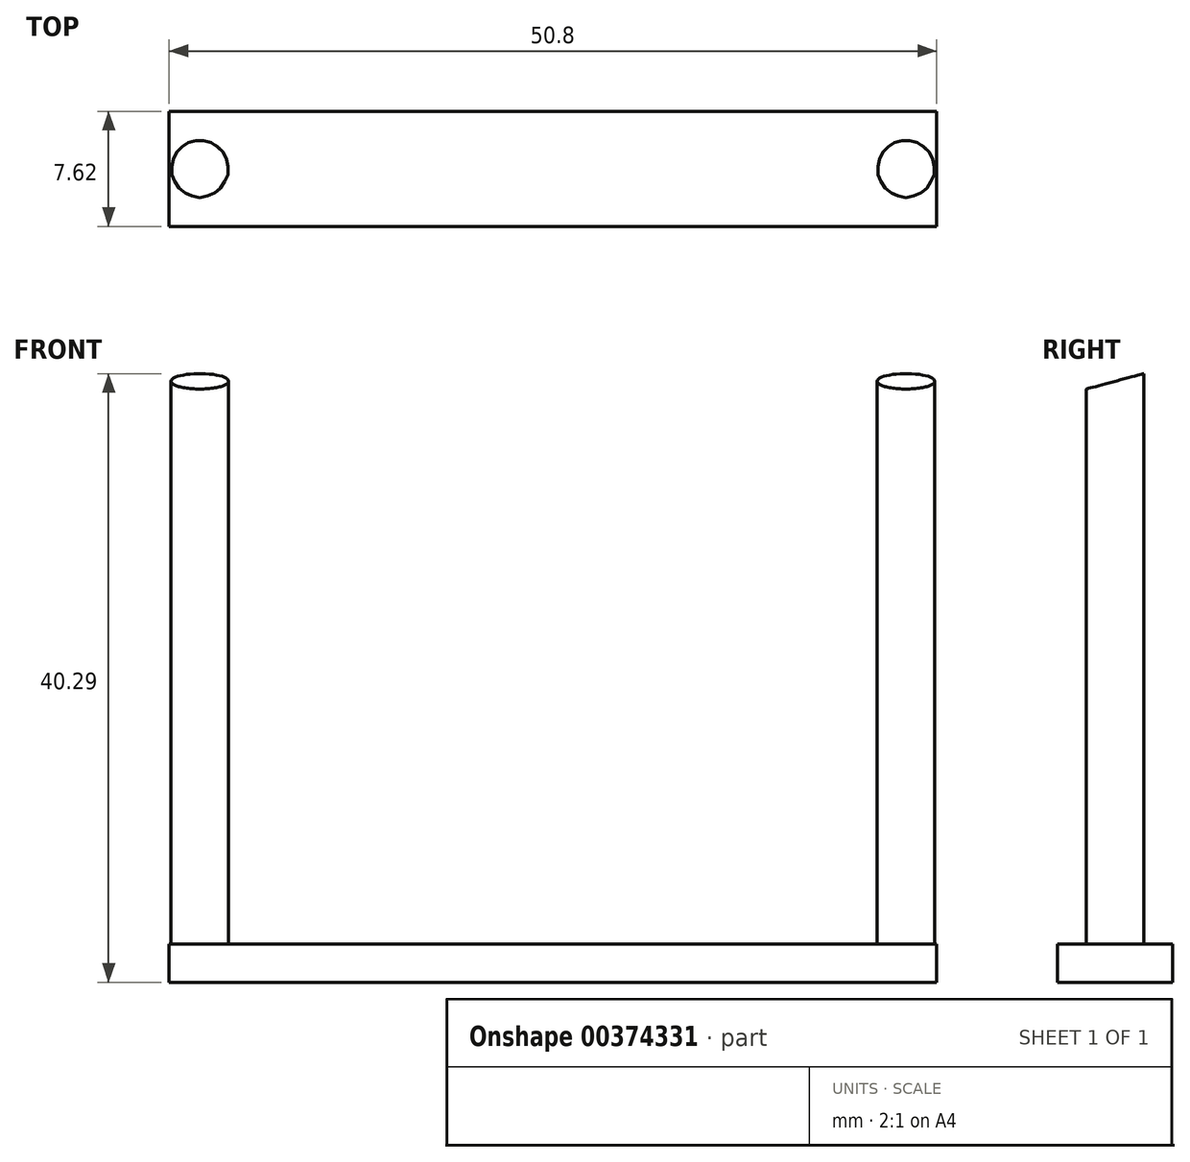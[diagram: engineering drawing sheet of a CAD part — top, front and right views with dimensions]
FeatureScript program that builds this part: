
annotation { "Feature Type Name" : "Feature", "Feature Type Description" : "" }
export const myFeature = defineFeature(function(context is Context, id is Id, definition is map)
    precondition{}
    {
        {
            var Q0;
            Q0=qCreatedBy(makeId("Top.planeOp"),FACE);
            var sketch = newSketch(context, id + "F0", { "sketchPlane" : qUnion([Q0])});
            skLineSegment(sketch, "E0.bottom", {"start": v(0, 0) * mm, "end": v(50.8, 0) * mm});
            skLineSegment(sketch, "E0.top", {"start": v(0, 7.62) * mm, "end": v(50.8, 7.62) * mm});
            skLineSegment(sketch, "E0.left", {"start": v(0, 0) * mm, "end": v(0, 7.62) * mm});
            skLineSegment(sketch, "E0.right", {"start": v(50.8, 0) * mm, "end": v(50.8, 7.62) * mm});
            skPoint(sketch, "E1.centerSnap0", {"position": v(50.8, 3.8) * mm});
            skSolve(sketch);
        }
        {
            var Q0;
            Q0 = qSketchRegion(id + "F0", true);
            extrude(context, id + "F1", {"entities" : qUnion([Q0]), "depth" : 2.54 * mm});
        }
        {
            var Q0;
            Q0=makeQuery(id+"F1.opExtrude","CAP_FACE",FACE,{"disambiguationData":[OSD([sQuery(id+"F0.wireOp",EDGE,"E0.bottom"),sQuery(id+"F0.wireOp",EDGE,"E0.top"),sQuery(id+"F0.wireOp",EDGE,"E0.left"),sQuery(id+"F0.wireOp",EDGE,"E0.right")])],"isStart":false});
            var sketch = newSketch(context, id + "F2", { "sketchPlane" : qUnion([Q0])});
            skCircle(sketch, "E2", {"center": v(2.03, 3.8) * mm, "radius": 1.9 * mm});
            skPoint(sketch, "E2.centerSnap0", {"position": v(0, 3.8) * mm});
            skCircle(sketch, "E3", {"center": v(48.77, 3.8) * mm, "radius": 1.9 * mm});
            skPoint(sketch, "E3.centerSnap0", {"position": v(50.8, 3.8) * mm});
            skSolve(sketch);
        }
        {
            var Q0;
            Q0 = qSketchRegion(id + "F2", true);
            extrude(context, id + "F3", {"entities" : qUnion([Q0]), "operationType" : NewBodyOperationType.ADD, "depth" : 38.1 * mm});
        }
        {
            var Q0;
            Q0=qCreatedBy(makeId("Right.planeOp"),FACE);
            var sketch = newSketch(context, id + "F4", { "sketchPlane" : qUnion([Q0])});
            skLineSegment(sketch, "E4", {"start": v(0, 38.76) * mm, "end": v(7.57, 40.8) * mm});
            skLineSegment(sketch, "E5", {"start": v(0, 38.76) * mm, "end": v(0, 40.64) * mm});
            skLineSegment(sketch, "E6", {"start": v(0, 40.64) * mm, "end": v(7.57, 40.8) * mm});
            skPoint(sketch, "E7.orphan", {"position": v(11.31, 40.86) * mm});
            skPoint(sketch, "E8.orphan", {"position": v(7.85, 40.86) * mm});
            skSolve(sketch);
        }
        {
            var Q0;
            Q0 = qSketchRegion(id + "F4", true);
            extrude(context, id + "F5", {"entities" : qUnion([Q0]), "operationType" : NewBodyOperationType.REMOVE, "endBound" : BoundingType.THROUGH_ALL, "depth" : 25.4 * mm, "hasSecondDirection" : true, "secondDirectionBound" : SecondDirectionBoundingType.THROUGH_ALL, "secondDirectionOppositeDirection" : true, "secondDirectionDepth" : 25.4 * mm});
        }
    });
